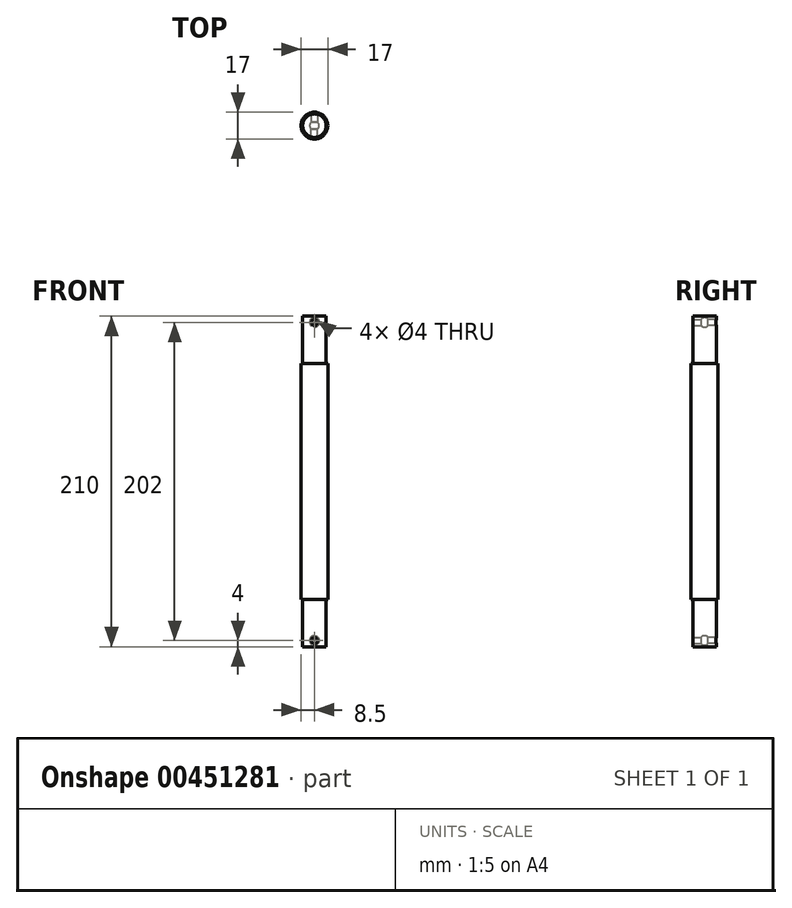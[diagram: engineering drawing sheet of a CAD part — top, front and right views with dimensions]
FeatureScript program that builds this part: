
annotation { "Feature Type Name" : "Feature", "Feature Type Description" : "" }
export const myFeature = defineFeature(function(context is Context, id is Id, definition is map)
    precondition{}
    {
        {
            var Q0;
            Q0=qCreatedBy(makeId("Front.planeOp"),FACE);
            var sketch = newSketch(context, id + "F0", { "sketchPlane" : qUnion([Q0])});
            skLineSegment(sketch, "E0", {"start": v(8.5, -75) * mm, "end": v(8.5, 75) * mm});
            skLineSegment(sketch, "E1", {"start": v(8.5, 75) * mm, "end": v(7.5, 75) * mm});
            skLineSegment(sketch, "E2", {"start": v(7.5, 75) * mm, "end": v(7.5, 105) * mm});
            skLineSegment(sketch, "E3", {"start": v(7.5, 105) * mm, "end": v(0, 105) * mm});
            skLineSegment(sketch, "E4", {"start": v(8.5, -75) * mm, "end": v(7.5, -75) * mm});
            skLineSegment(sketch, "E5", {"start": v(7.5, -75) * mm, "end": v(7.5, -105) * mm});
            skLineSegment(sketch, "E6", {"start": v(7.5, -105) * mm, "end": v(0, -105) * mm});
            skLineSegment(sketch, "E7", {"start": v(0, -105) * mm, "end": v(0, 105) * mm});
            skLineSegment(sketch, "E8", {"start": v(0, 0) * mm, "end": v(0, 128.44) * mm, "construction": true});
            skArc(sketch, "E9", {"start": v(0, 104) * mm, "mid": v(3, 101) * mm, "end": v(0, 98) * mm});
            skArc(sketch, "E10.MirrorCS", {"start": v(0, 104) * mm, "mid": v(-3, 101) * mm, "end": v(0, 98) * mm});
            skLineSegment(sketch, "E11", {"start": v(-46.57, 0) * mm, "end": v(63.2, 0) * mm, "construction": true});
            skPoint(sketch, "E11.endSnap0", {"position": v(8.5, 0) * mm});
            skArc(sketch, "E12.MirrorCS", {"start": v(0, -104) * mm, "mid": v(3, -101) * mm, "end": v(0, -98) * mm});
            skArc(sketch, "E13.MirrorCS", {"start": v(0, -104) * mm, "mid": v(-3, -101) * mm, "end": v(0, -98) * mm});
            skSolve(sketch);
        }
        {
            var Q0;
            Q0=makeQuery(id+"F0.imprint","IMPRINT",FACE,{"disambiguationData":[TD([[makeQuery(id+"F0.imprint","IMPRINT",EDGE,{"derivedFrom":sQuery(id+"F0.wireOp",EDGE,"E0")}),1.0]])]});
            var Q1;
            Q1=sQuery(id+"F0.wireOp",EDGE,"E8");
            revolve(context, id + "F1", {"entities" : qUnion([Q0]), "axis" : qUnion([Q1]), "revolveType" : RevolveType.FULL});
        }
        {
            var Q0;
            Q0=sQuery(id+"F0.wireOp",VERTEX,"E10.MirrorCS.center");
            var Q1;
            Q1=makeQuery(id+"F1.opRevolve","SWEPT_BODY",BODY,{"disambiguationData":[OSD([sQuery(id+"F0.wireOp",EDGE,"E0"),sQuery(id+"F0.wireOp",EDGE,"E1"),sQuery(id+"F0.wireOp",EDGE,"E2"),sQuery(id+"F0.wireOp",EDGE,"E3"),sQuery(id+"F0.wireOp",EDGE,"E4"),sQuery(id+"F0.wireOp",EDGE,"E5"),sQuery(id+"F0.wireOp",EDGE,"E6"),sQuery(id+"F0.wireOp",EDGE,"E7"),sQuery(id+"F0.wireOp",EDGE,"E9")])]});
            hole(context, id + "F2", {"style" : HoleStyle.SIMPLE, "endStyle" : HoleEndStyle.THROUGH, "holeDiameter" : 4 * mm, "isTappedThrough" : true, "tappedDepth" : 12 * mm, "tapClearance" : 3, "locations" : qUnion([Q0]), "scope" : qUnion([Q1])});
        }
        {
            var Q0;
            Q0=sQuery(id+"F0.wireOp",VERTEX,"E10.MirrorCS.center");
            var Q1;
            Q1=makeQuery(id+"F1.opRevolve","SWEPT_BODY",BODY,{"disambiguationData":[OSD([sQuery(id+"F0.wireOp",EDGE,"E0"),sQuery(id+"F0.wireOp",EDGE,"E1"),sQuery(id+"F0.wireOp",EDGE,"E2"),sQuery(id+"F0.wireOp",EDGE,"E3"),sQuery(id+"F0.wireOp",EDGE,"E4"),sQuery(id+"F0.wireOp",EDGE,"E5"),sQuery(id+"F0.wireOp",EDGE,"E6"),sQuery(id+"F0.wireOp",EDGE,"E7"),sQuery(id+"F0.wireOp",EDGE,"E9")])]});
            hole(context, id + "F3", {"style" : HoleStyle.SIMPLE, "endStyle" : HoleEndStyle.THROUGH, "oppositeDirection" : true, "holeDiameter" : 4 * mm, "isTappedThrough" : true, "tappedDepth" : 12 * mm, "tapClearance" : 3, "locations" : qUnion([Q0]), "scope" : qUnion([Q1])});
        }
        {
            var Q0;
            Q0=sQuery(id+"F0.wireOp",VERTEX,"E13.MirrorCS.center");
            var Q1;
            Q1=makeQuery(id+"F1.opRevolve","SWEPT_BODY",BODY,{"disambiguationData":[OSD([sQuery(id+"F0.wireOp",EDGE,"E0"),sQuery(id+"F0.wireOp",EDGE,"E1"),sQuery(id+"F0.wireOp",EDGE,"E2"),sQuery(id+"F0.wireOp",EDGE,"E3"),sQuery(id+"F0.wireOp",EDGE,"E4"),sQuery(id+"F0.wireOp",EDGE,"E5"),sQuery(id+"F0.wireOp",EDGE,"E6"),sQuery(id+"F0.wireOp",EDGE,"E7"),sQuery(id+"F0.wireOp",EDGE,"E9"),sQuery(id+"F0.wireOp",EDGE,"E12.MirrorCS")])]});
            hole(context, id + "F4", {"style" : HoleStyle.SIMPLE, "endStyle" : HoleEndStyle.BLIND, "oppositeDirection" : true, "holeDiameter" : 4 * mm, "holeDepth" : 150 * mm, "isTappedThrough" : true, "tappedDepth" : 12 * mm, "tapClearance" : 3, "locations" : qUnion([Q0]), "scope" : qUnion([Q1])});
        }
        {
            var Q0;
            Q0=sQuery(id+"F0.wireOp",VERTEX,"E13.MirrorCS.center");
            var Q1;
            Q1=makeQuery(id+"F1.opRevolve","SWEPT_BODY",BODY,{"disambiguationData":[OSD([sQuery(id+"F0.wireOp",EDGE,"E0"),sQuery(id+"F0.wireOp",EDGE,"E1"),sQuery(id+"F0.wireOp",EDGE,"E2"),sQuery(id+"F0.wireOp",EDGE,"E3"),sQuery(id+"F0.wireOp",EDGE,"E4"),sQuery(id+"F0.wireOp",EDGE,"E5"),sQuery(id+"F0.wireOp",EDGE,"E6"),sQuery(id+"F0.wireOp",EDGE,"E7"),sQuery(id+"F0.wireOp",EDGE,"E9"),sQuery(id+"F0.wireOp",EDGE,"E12.MirrorCS")])]});
            hole(context, id + "F5", {"style" : HoleStyle.SIMPLE, "endStyle" : HoleEndStyle.BLIND, "holeDiameter" : 4 * mm, "holeDepth" : 150 * mm, "isTappedThrough" : true, "tappedDepth" : 12 * mm, "tapClearance" : 3, "locations" : qUnion([Q0]), "scope" : qUnion([Q1])});
        }
    });
